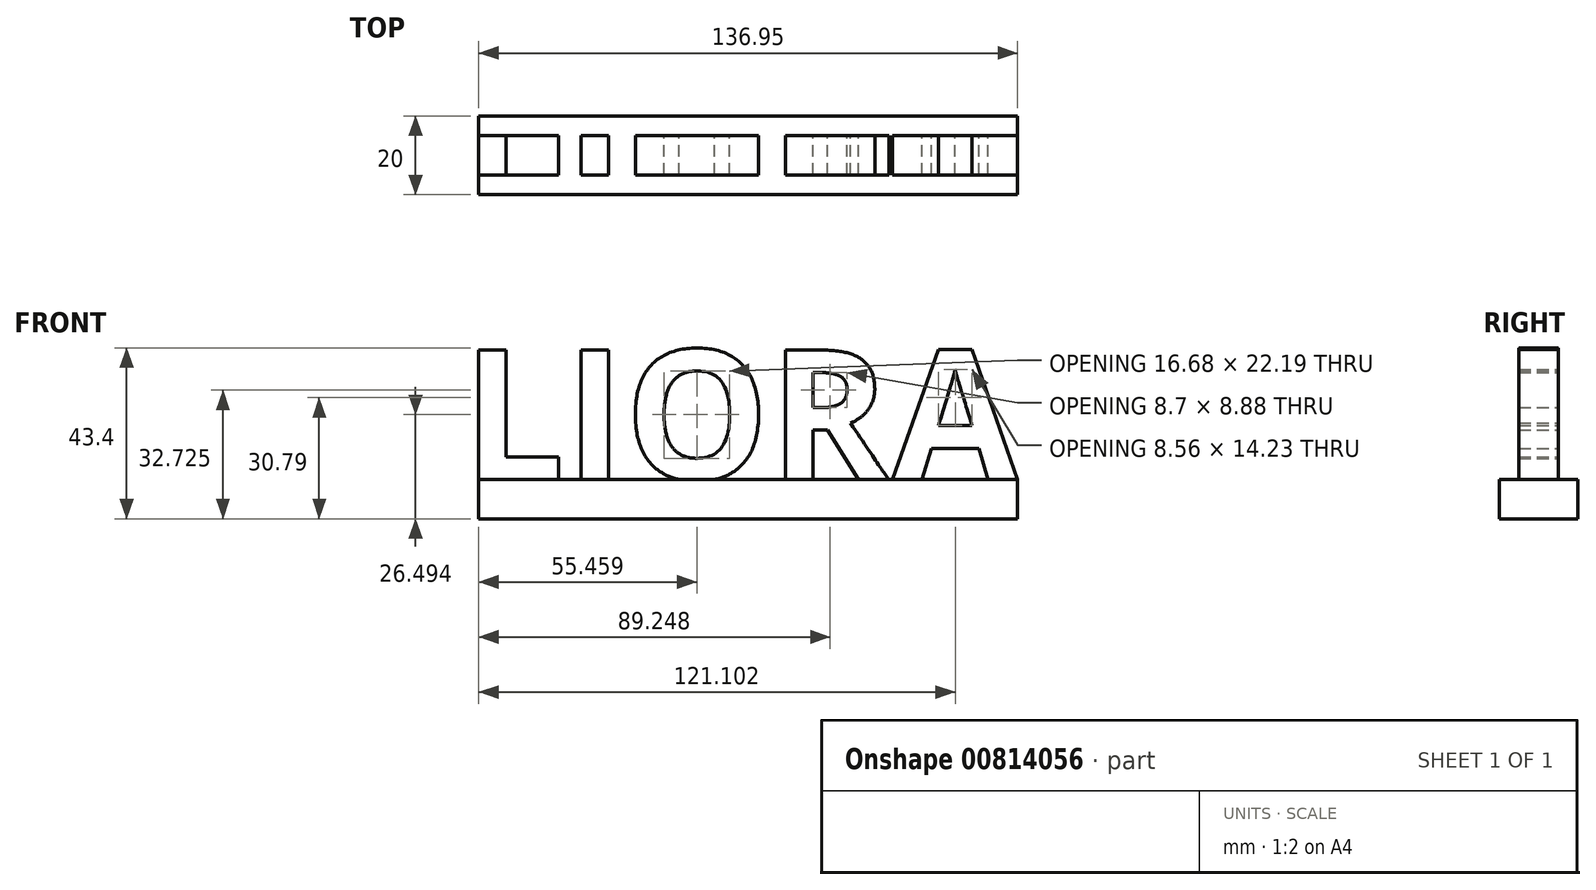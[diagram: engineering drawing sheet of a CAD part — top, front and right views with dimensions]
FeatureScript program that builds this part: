
annotation { "Feature Type Name" : "Feature", "Feature Type Description" : "" }
export const myFeature = defineFeature(function(context is Context, id is Id, definition is map)
    precondition{}
    {
        {
            var Q0;
            Q0=qCreatedBy(makeId("Front.planeOp"),FACE);
            var sketch = newSketch(context, id + "F0", { "sketchPlane" : qUnion([Q0])});
            skText(sketch, "E0", { "text": "LIORA", "fontName": "OpenSans-Bold.ttf"});
            const initialGuessF0  = {"E0": [-0.0745, 0, 1, 0, 0.03316]};
            skSetInitialGuess(sketch, initialGuessF0);
            skSolve(sketch);
        }
        {
            var Q0;
            Q0 = qSketchRegion(id + "F0", true);
            extrude(context, id + "F1", {"entities" : qUnion([Q0]), "depth" : 10 * mm, "offsetDistance" : 25 * mm});
        }
        {
            var Q0;
            Q0=makeQuery(id+"F1.opExtrude","SWEPT_FACE",FACE,{"disambiguationData":[OSD([sQuery(id+"F0.wireOp",EDGE,"E0.sketch_text.stroke-5")])]});
            var sketch = newSketch(context, id + "F2", { "sketchPlane" : qUnion([Q0])});
            skLineSegment(sketch, "E1.bottom", {"start": v(-70.36, 15) * mm, "end": v(66.58, 15) * mm});
            skLineSegment(sketch, "E1.top", {"start": v(-70.36, -5) * mm, "end": v(66.58, -5) * mm});
            skLineSegment(sketch, "E1.left", {"start": v(-70.36, 15) * mm, "end": v(-70.36, -5) * mm});
            skLineSegment(sketch, "E1.right", {"start": v(66.58, 15) * mm, "end": v(66.58, -5) * mm});
            skSolve(sketch);
        }
        {
            var Q0;
            Q0 = qSketchRegion(id + "F2", true);
            extrude(context, id + "F3", {"entities" : qUnion([Q0]), "operationType" : NewBodyOperationType.ADD, "depth" : 10 * mm, "offsetDistance" : 25 * mm});
        }
    });
